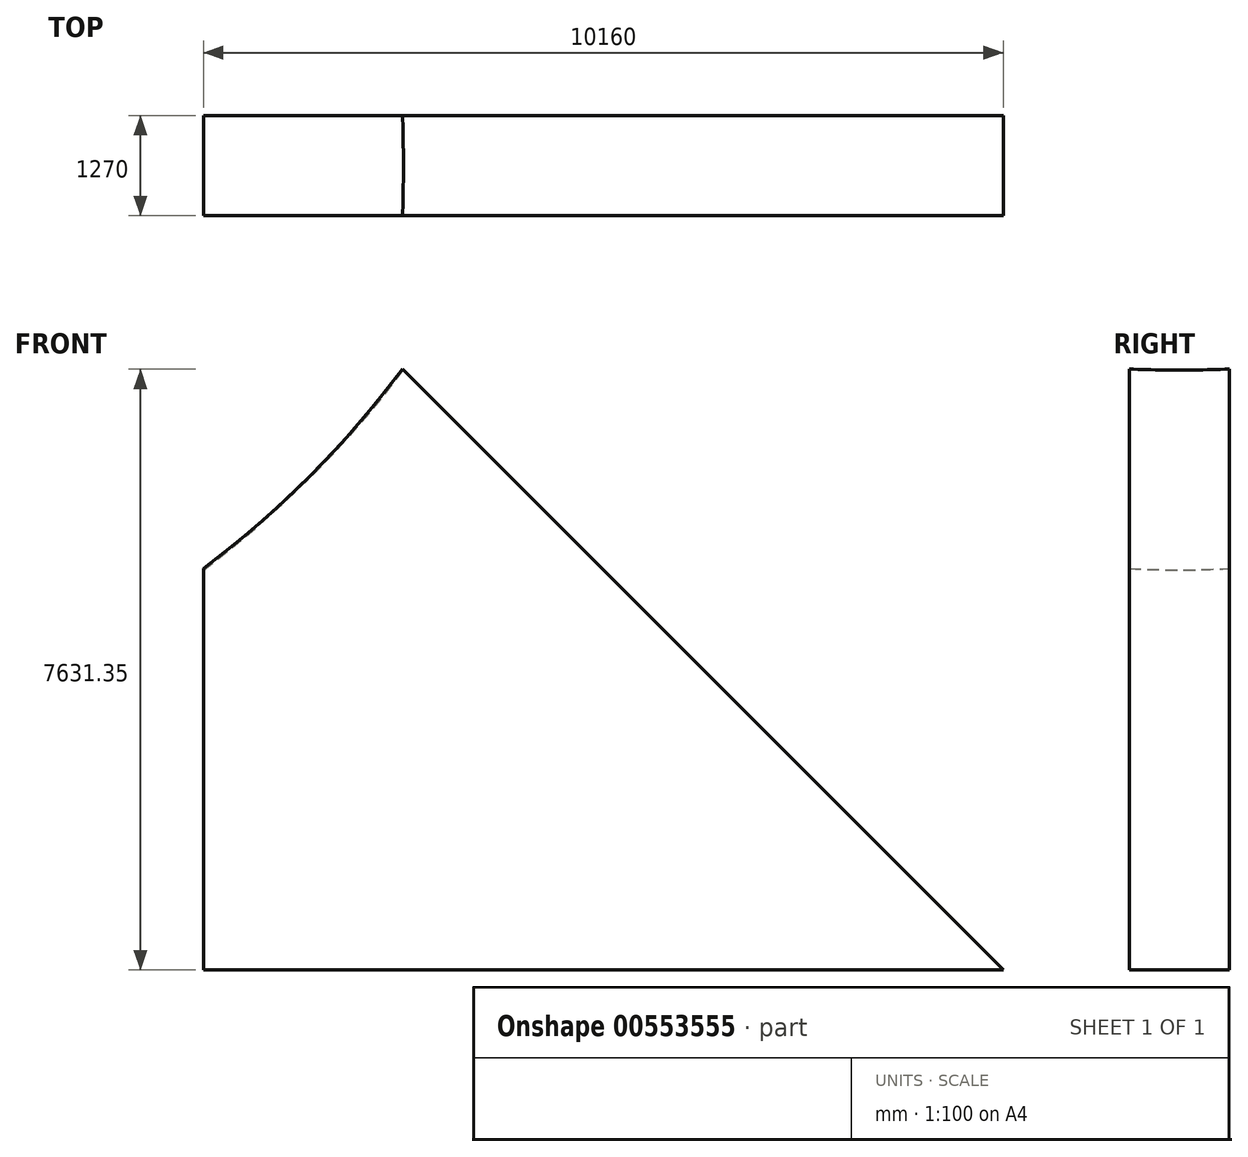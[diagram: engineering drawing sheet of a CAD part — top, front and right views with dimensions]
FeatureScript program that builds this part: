
annotation { "Feature Type Name" : "Feature", "Feature Type Description" : "" }
export const myFeature = defineFeature(function(context is Context, id is Id, definition is map)
    precondition{}
    {
        {
            var Q0;
            Q0=qCreatedBy(makeId("Front.planeOp"),FACE);
            var sketch = newSketch(context, id + "F0", { "sketchPlane" : qUnion([Q0])});
            skLineSegment(sketch, "E0", {"start": v(0, 0) * mm, "end": v(10160, 0) * mm});
            skLineSegment(sketch, "E1", {"start": v(10160, 0) * mm, "end": v(0, 10160) * mm});
            skLineSegment(sketch, "E2", {"start": v(0, 10160) * mm, "end": v(0, 0) * mm});
            skSolve(sketch);
        }
        {
            var Q0;
            Q0 = qSketchRegion(id + "F0", true);
            extrude(context, id + "F1", {"entities" : qUnion([Q0]), "endBound" : BoundingType.SYMMETRIC, "depth" : 1270 * mm, "offsetDistance" : 25.4 * mm});
        }
        {
            var Q0;
            Q0=qCreatedBy(makeId("Front.planeOp"),FACE);
            var sketch = newSketch(context, id + "F2", { "sketchPlane" : qUnion([Q0])});
            skArc(sketch, "E3", {"start": v(-20320, 15240) * mm, "mid": v(-7620, 2540) * mm, "end": v(5080, 15240) * mm});
            skLineSegment(sketch, "E4", {"start": v(5080, 15240) * mm, "end": v(-20320, 15240) * mm});
            skLineSegment(sketch, "E5", {"start": v(-7620, 15240) * mm, "end": v(13626.1, 15240) * mm, "construction": true});
            skSolve(sketch);
        }
        {
            var Q0;
            Q0=makeQuery(id+"F2.imprint","IMPRINT",FACE,{"disambiguationData":[TD([[makeQuery(id+"F2.imprint","IMPRINT",EDGE,{"derivedFrom":sQuery(id+"F2.wireOp",EDGE,"E3")}),1.0]])]});
            var Q1;
            Q1=sQuery(id+"F2.wireOp",EDGE,"E5");
            revolve(context, id + "F3", {"operationType" : NewBodyOperationType.REMOVE, "entities" : qUnion([Q0]), "axis" : qUnion([Q1]), "revolveType" : RevolveType.FULL});
        }
    });
